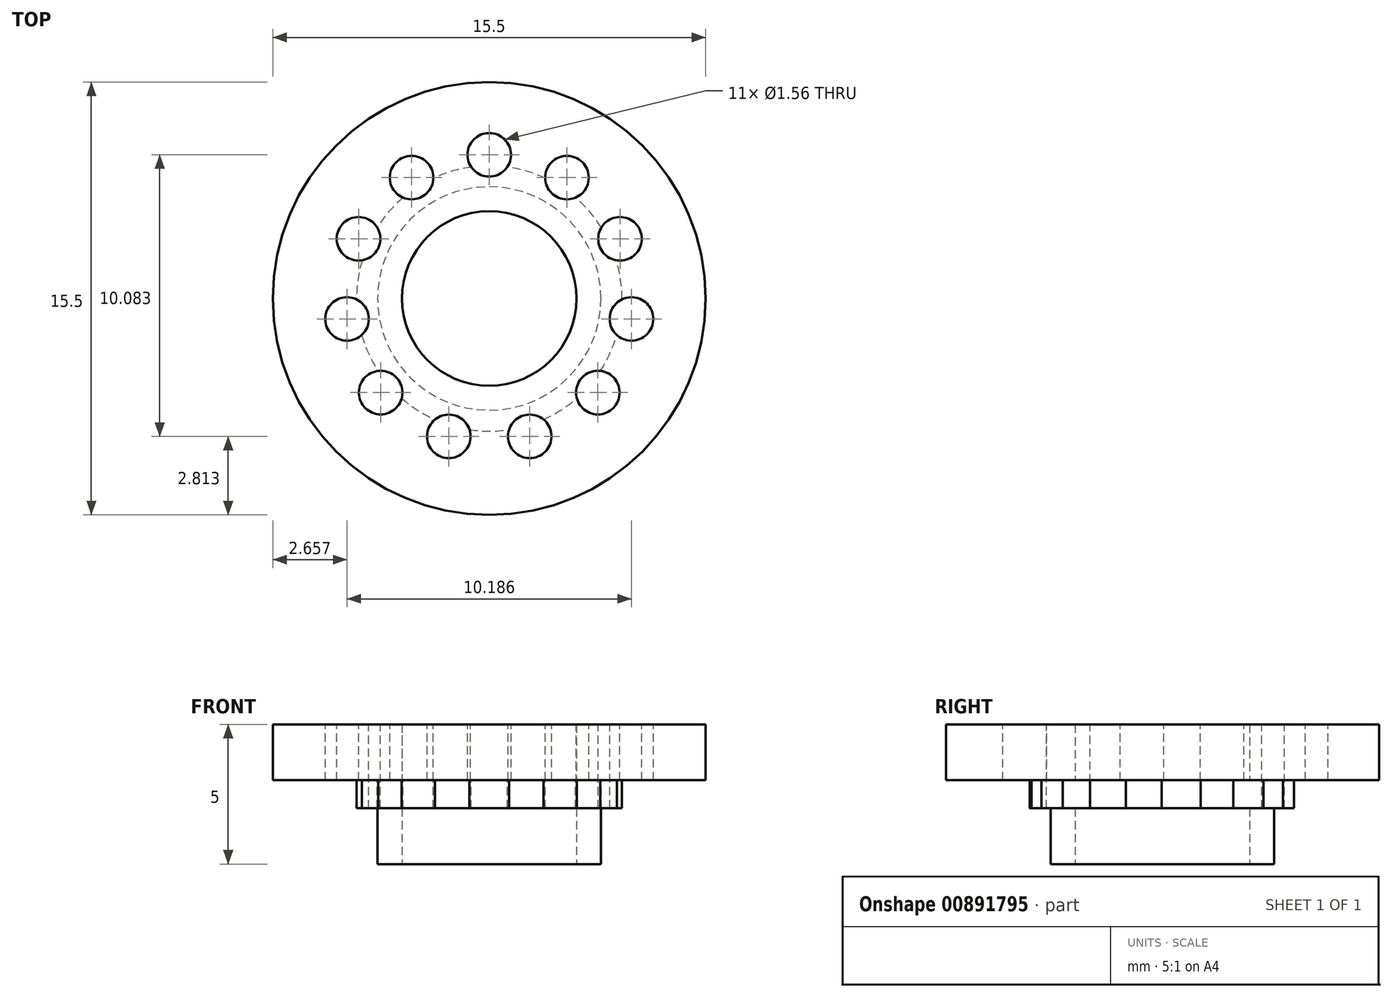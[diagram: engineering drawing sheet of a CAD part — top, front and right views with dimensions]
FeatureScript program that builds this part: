
annotation { "Feature Type Name" : "Feature", "Feature Type Description" : "" }
export const myFeature = defineFeature(function(context is Context, id is Id, definition is map)
    precondition{}
    {
        {
            var Q0;
            Q0=qCreatedBy(makeId("Top.planeOp"),FACE);
            var sketch = newSketch(context, id + "F0", { "sketchPlane" : qUnion([Q0])});
            skCircle(sketch, "E0", {"center": v(0, 0) * mm, "radius": 4 * mm});
            skCircle(sketch, "E1", {"center": v(0, 0) * mm, "radius": 3.12 * mm});
            skSolve(sketch);
        }
        {
            var Q0;
            Q0=makeQuery(id+"F0.imprint","IMPRINT",FACE,{"disambiguationData":[TD([[makeQuery(id+"F0.imprint","IMPRINT",EDGE,{"derivedFrom":sQuery(id+"F0.wireOp",EDGE,"E0")}),1.0]])]});
            extrude(context, id + "F1", {"entities" : qUnion([Q0]), "depth" : 5 * mm, "offsetDistance" : 25.4 * mm});
        }
        {
            var Q0;
            Q0=makeQuery(id+"F1.opExtrude","CAP_FACE",FACE,{"disambiguationData":[OSD([sQuery(id+"F0.wireOp",EDGE,"E0"),sQuery(id+"F0.wireOp",EDGE,"E1")])],"isStart":false});
            var sketch = newSketch(context, id + "F2", { "sketchPlane" : qUnion([Q0])});
            skCircle(sketch, "E2", {"center": v(0, 0) * mm, "radius": 3.95 * mm});
            skCircle(sketch, "E3", {"center": v(0, 0) * mm, "radius": 7.75 * mm});
            skSolve(sketch);
        }
        {
            var Q0;
            Q0=makeQuery(id+"F2.imprint","IMPRINT",FACE,{"disambiguationData":[TD([[makeQuery(id+"F2.imprint","IMPRINT",EDGE,{"derivedFrom":sQuery(id+"F2.wireOp",EDGE,"E3")}),1.0]])]});
            extrude(context, id + "F3", {"entities" : qUnion([Q0]), "operationType" : NewBodyOperationType.ADD, "oppositeDirection" : true, "depth" : 2 * mm, "offsetDistance" : 25.4 * mm});
        }
        {
            var Q0;
            Q0=makeQuery(id+"F3.opExtrude","CAP_FACE",FACE,{"disambiguationData":[OSD([sQuery(id+"F0.wireOp",EDGE,"E0"),sQuery(id+"F2.wireOp",EDGE,"E3")])],"isStart":false});
            var sketch = newSketch(context, id + "F4", { "sketchPlane" : qUnion([Q0])});
            skCircle(sketch, "E4", {"center": v(0, 0) * mm, "radius": 4.75 * mm});
            skSolve(sketch);
        }
        {
            var Q0;
            Q0=makeQuery(id+"F4.imprint","IMPRINT",FACE,{"disambiguationData":[TD([[makeQuery(id+"F4.imprint","IMPRINT",EDGE,{"derivedFrom":sQuery(id+"F4.wireOp",EDGE,"E4")}),1.0]])]});
            extrude(context, id + "F5", {"entities" : qUnion([Q0]), "operationType" : NewBodyOperationType.ADD, "depth" : 1 * mm, "offsetDistance" : 25.4 * mm});
        }
        {
            var Q0;
            {var subQ0=sQuery(id+"F0.wireOp",EDGE,"E0");Q0=makeQuery(id+"F3.boolean.opBoolean","MERGE",FACE,{"derivedFrom":[makeQuery(id+"F1.opExtrude","CAP_FACE",FACE,{"disambiguationData":[OSD([subQ0,sQuery(id+"F0.wireOp",EDGE,"E1")])],"isStart":false}),makeQuery(id+"F3.opExtrude","CAP_FACE",FACE,{"disambiguationData":[OSD([subQ0,sQuery(id+"F2.wireOp",EDGE,"E3")])],"isStart":true})]});}
            var sketch = newSketch(context, id + "F6", { "sketchPlane" : qUnion([Q0])});
            skCircle(sketch, "E5", {"center": v(0, 5.15) * mm, "radius": 0.78 * mm});
            skCircle(sketch, "E6.1.0", {"center": v(-2.78, 4.33) * mm, "radius": 0.78 * mm});
            skCircle(sketch, "E6.2.0", {"center": v(-4.68, 2.14) * mm, "radius": 0.78 * mm});
            skCircle(sketch, "E6.3.0", {"center": v(-5.1, -0.73) * mm, "radius": 0.78 * mm});
            skCircle(sketch, "E6.4.0", {"center": v(-3.89, -3.37) * mm, "radius": 0.78 * mm});
            skCircle(sketch, "E6.5.0", {"center": v(-1.45, -4.94) * mm, "radius": 0.78 * mm});
            skCircle(sketch, "E6.6.0", {"center": v(1.45, -4.94) * mm, "radius": 0.78 * mm});
            skCircle(sketch, "E6.7.0", {"center": v(3.89, -3.37) * mm, "radius": 0.78 * mm});
            skCircle(sketch, "E6.8.0", {"center": v(5.1, -0.73) * mm, "radius": 0.78 * mm});
            skCircle(sketch, "E6.9.0", {"center": v(4.68, 2.14) * mm, "radius": 0.78 * mm});
            skCircle(sketch, "E6.10.0", {"center": v(2.78, 4.33) * mm, "radius": 0.78 * mm});
            skPoint(sketch, "E6.center", {"position": v(0, 0) * mm});
            skSolve(sketch);
        }
        {
            var Q0;
            Q0 = qSketchRegion(id + "F6", true);
            extrude(context, id + "F7", {"entities" : qUnion([Q0]), "operationType" : NewBodyOperationType.REMOVE, "endBound" : BoundingType.SYMMETRIC, "oppositeDirection" : true, "depth" : 25.4 * mm, "offsetDistance" : 25.4 * mm});
        }
    });
